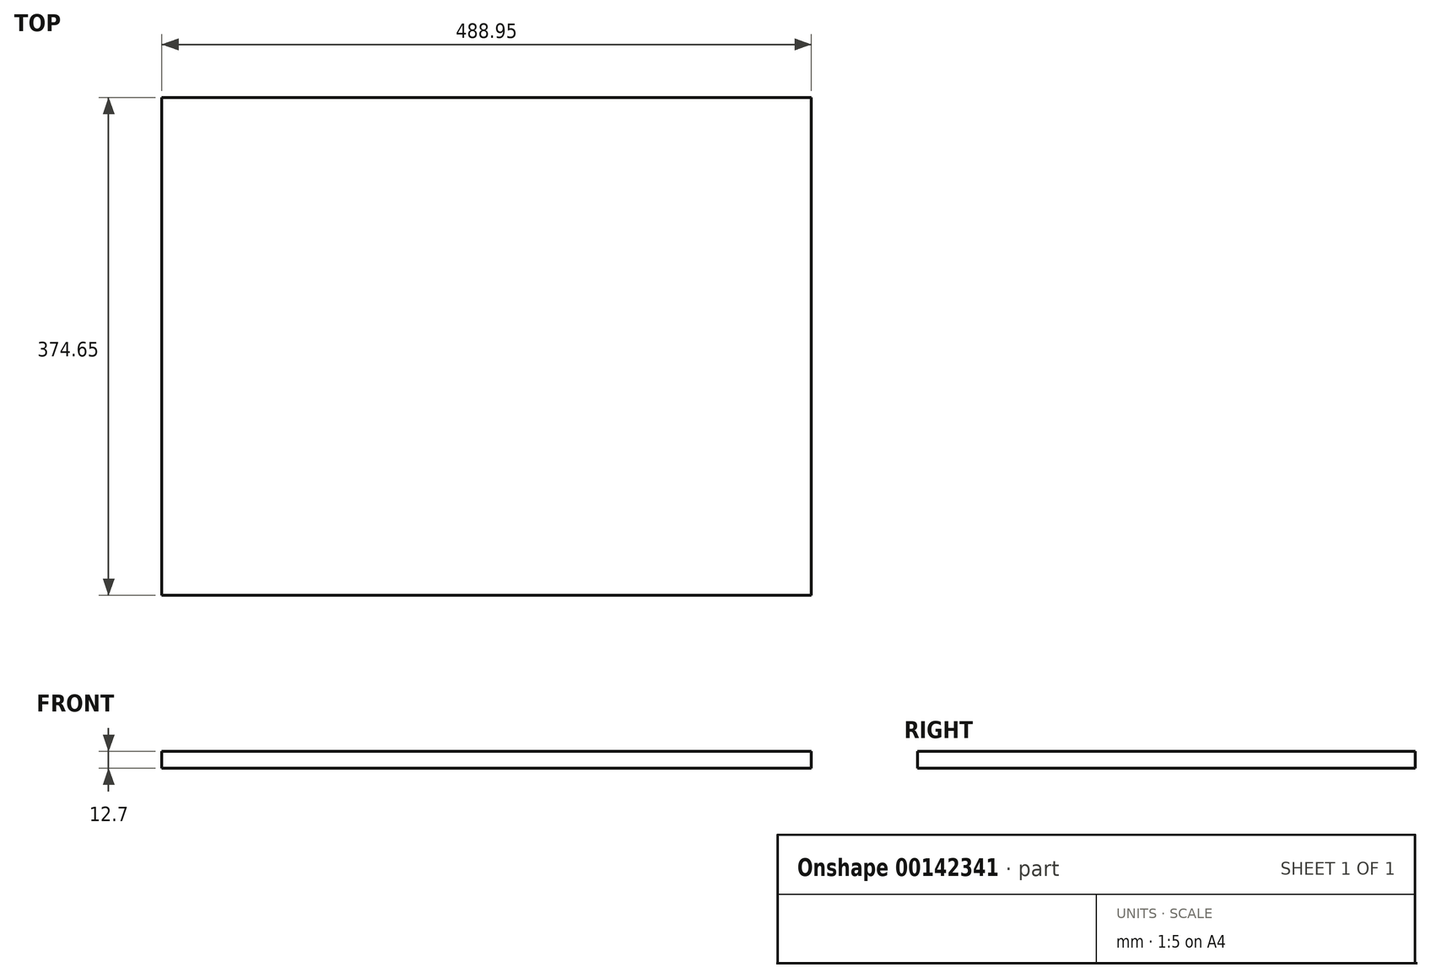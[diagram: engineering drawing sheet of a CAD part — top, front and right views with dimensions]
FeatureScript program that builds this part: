
annotation { "Feature Type Name" : "Feature", "Feature Type Description" : "" }
export const myFeature = defineFeature(function(context is Context, id is Id, definition is map)
    precondition{}
    {
        {
            var Q0;
            Q0=qCreatedBy(makeId("Top.planeOp"),FACE);
            var sketch = newSketch(context, id + "F0", { "sketchPlane" : qUnion([Q0])});
            skLineSegment(sketch, "E0.bottom", {"start": v(-276.38, 165.02) * mm, "end": v(212.57, 165.02) * mm});
            skLineSegment(sketch, "E0.top", {"start": v(-276.38, -209.63) * mm, "end": v(212.57, -209.63) * mm});
            skLineSegment(sketch, "E0.left", {"start": v(-276.38, 165.02) * mm, "end": v(-276.38, -209.63) * mm});
            skLineSegment(sketch, "E0.right", {"start": v(212.57, 165.02) * mm, "end": v(212.57, -209.63) * mm});
            skSolve(sketch);
        }
        {
            var Q0;
            Q0=makeQuery(id+"F0.imprint","IMPRINT",FACE,{"disambiguationData":[TD([[makeQuery(id+"F0.imprint","IMPRINT",EDGE,{"derivedFrom":sQuery(id+"F0.wireOp",EDGE,"E0.bottom")}),-1.0]])]});
            extrude(context, id + "F1", {"entities" : qUnion([Q0]), "depth" : 12.7 * mm});
        }
    });
